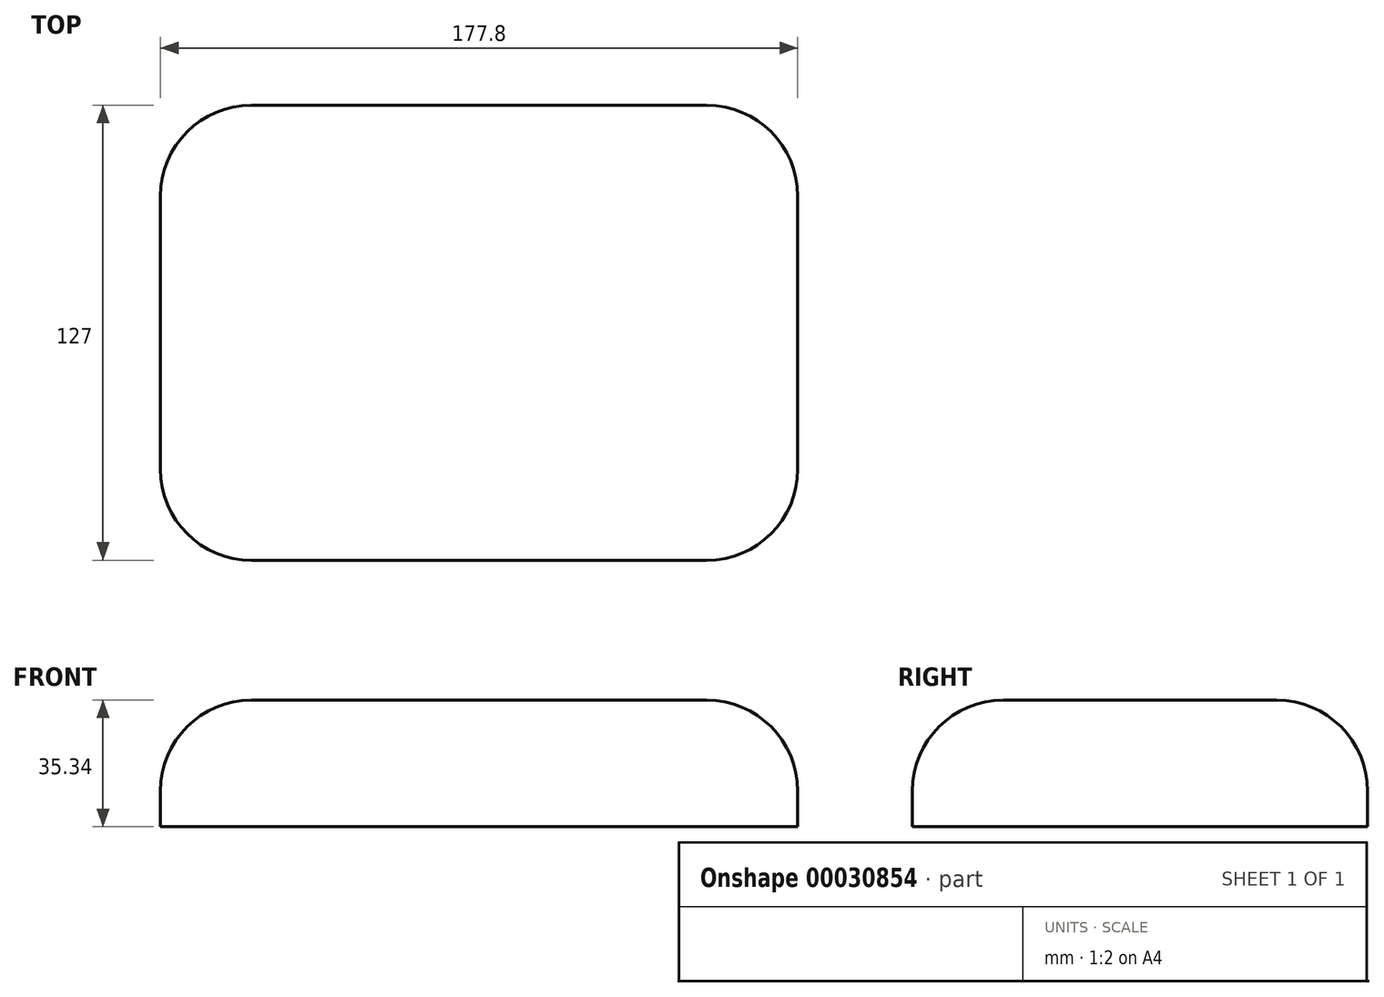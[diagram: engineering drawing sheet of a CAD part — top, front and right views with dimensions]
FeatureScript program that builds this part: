
annotation { "Feature Type Name" : "Feature", "Feature Type Description" : "" }
export const myFeature = defineFeature(function(context is Context, id is Id, definition is map)
    precondition{}
    {
        {
            var Q0;
            Q0=qCreatedBy(makeId("Right.planeOp"),FACE);
            var sketch = newSketch(context, id + "F0", { "sketchPlane" : qUnion([Q0])});
            skLineSegment(sketch, "E0", {"start": v(-68.96, 47.55) * mm, "end": v(58.04, 47.55) * mm});
            skLineSegment(sketch, "E1", {"start": v(-68.96, 47.55) * mm, "end": v(-68.96, 12.21) * mm});
            skLineSegment(sketch, "E2", {"start": v(58.04, 47.55) * mm, "end": v(58.04, 12.21) * mm});
            skLineSegment(sketch, "E3", {"start": v(58.04, 12.21) * mm, "end": v(-68.96, 12.21) * mm});
            skSolve(sketch);
        }
        {
            var Q0;
            Q0 = qSketchRegion(id + "F0", true);
            extrude(context, id + "F1", {"entities" : qUnion([Q0]), "endBound" : BoundingType.SYMMETRIC, "depth" : 177.8 * mm});
        }
        {
            var Q0;
            Q0=makeQuery(id+"F1.opExtrude","CAP_EDGE",EDGE,{"disambiguationData":[OSD([sQuery(id+"F0.wireOp",EDGE,"E0")])],"isStart":true});
            fillet(context, id + "F2", {"entities" : qUnion([Q0]), "radius" : 25.4 * mm, "tangentPropagation" : true, "allowEdgeOverflow" : false});
        }
        {
            var Q0;
            Q0=makeQuery(id+"F1.opExtrude","CAP_EDGE",EDGE,{"disambiguationData":[OSD([sQuery(id+"F0.wireOp",EDGE,"E0")])],"isStart":false});
            fillet(context, id + "F3", {"entities" : qUnion([Q0]), "radius" : 25.4 * mm, "tangentPropagation" : true, "allowEdgeOverflow" : false});
        }
        {
            var Q0;
            Q0=makeQuery(id+"F1.opExtrude","CAP_EDGE",EDGE,{"disambiguationData":[OSD([sQuery(id+"F0.wireOp",EDGE,"E2")])],"isStart":true});
            fillet(context, id + "F4", {"entities" : qUnion([Q0]), "radius" : 25.4 * mm, "tangentPropagation" : true, "allowEdgeOverflow" : false});
        }
        {
            var Q0;
            Q0=makeQuery(id+"F1.opExtrude","CAP_EDGE",EDGE,{"disambiguationData":[OSD([sQuery(id+"F0.wireOp",EDGE,"E1")])],"isStart":true});
            fillet(context, id + "F5", {"entities" : qUnion([Q0]), "radius" : 25.4 * mm, "tangentPropagation" : true, "allowEdgeOverflow" : false});
        }
    });
